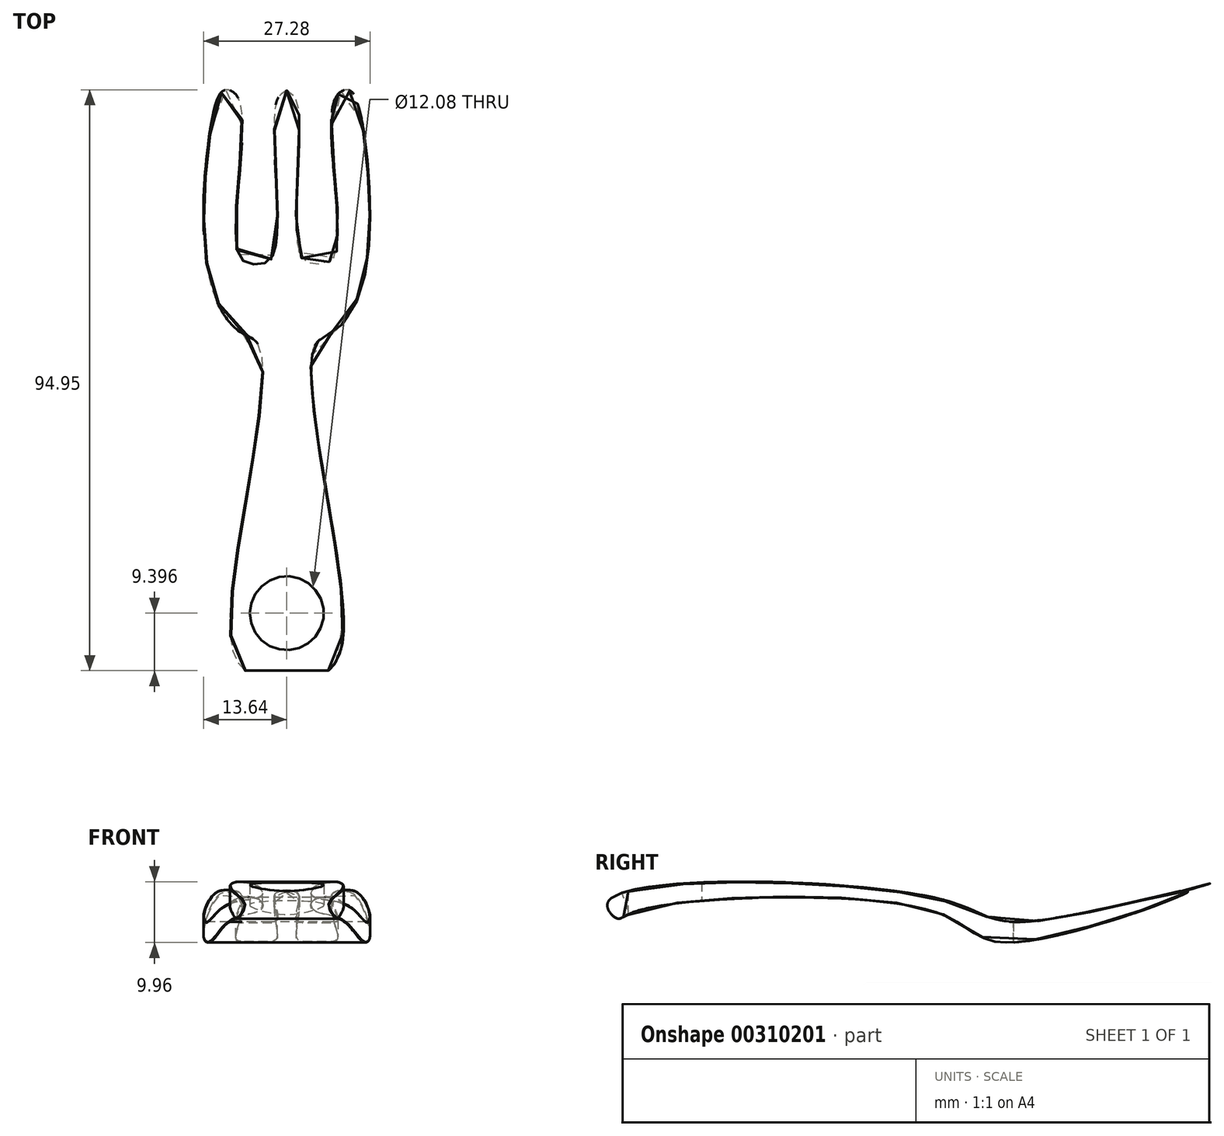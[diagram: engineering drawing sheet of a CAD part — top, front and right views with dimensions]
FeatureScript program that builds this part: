
annotation { "Feature Type Name" : "Feature", "Feature Type Description" : "" }
export const myFeature = defineFeature(function(context is Context, id is Id, definition is map)
    precondition{}
    {
        {
            var Q0;
            Q0=qCreatedBy(makeId("Top.planeOp"),FACE);
            var sketch = newSketch(context, id + "F0", { "sketchPlane" : qUnion([Q0])});
            skLineSegment(sketch, "E0.bottom", {"start": v(15, -50) * mm, "end": v(-15, -50) * mm});
            skLineSegment(sketch, "E0.top", {"start": v(15, 50) * mm, "end": v(-15, 50) * mm});
            skLineSegment(sketch, "E0.left", {"start": v(15, -50) * mm, "end": v(15, 50) * mm});
            skLineSegment(sketch, "E0.right", {"start": v(-15, -50) * mm, "end": v(-15, 50) * mm});
            skPoint(sketch, "E0.middle", {"position": v(0, 0) * mm});
            skSolve(sketch);
        }
        {
            var Q0;
            Q0=makeQuery(id+"F0.imprint","IMPRINT",FACE,{"disambiguationData":[TD([[makeQuery(id+"F0.imprint","IMPRINT",EDGE,{"derivedFrom":sQuery(id+"F0.wireOp",EDGE,"E0.bottom")}),-1.0]])]});
            extrude(context, id + "F1", {"entities" : qUnion([Q0]), "depth" : 30 * mm});
        }
        {
            var Q0;
            Q0=makeQuery(id+"F1.opExtrude","CAP_FACE",FACE,{"disambiguationData":[OSD([sQuery(id+"F0.wireOp",EDGE,"E0.bottom"),sQuery(id+"F0.wireOp",EDGE,"E0.top"),sQuery(id+"F0.wireOp",EDGE,"E0.left"),sQuery(id+"F0.wireOp",EDGE,"E0.right")])],"isStart":false});
            var sketch = newSketch(context, id + "F2", { "sketchPlane" : qUnion([Q0])});
            skFitSpline(sketch, "E1.MirrorCS", {"points": [v(0, 47.97) * mm, v(-1.83, 45.53) * mm, v(-2.18, 21.21) * mm, v(-5.06, 19.56) * mm, v(-7.93, 21.3) * mm, v(-7.58, 45.7) * mm, v(-9.94, 48.05) * mm, v(-11.6, 45.87) * mm, v(-12.99, 18.77) * mm, v(-7.5, 8.4) * mm, v(-4.36, 5.7) * mm, v(-8.88, -33.02) * mm, v(-7.12, -46.63) * mm, v(0, -49.34) * mm], "startDerivative": vector(-53.96, -27.16) * mm, "endDerivative": vector(122.77, -35.87) * mm});
            skLineSegment(sketch, "E2", {"start": v(-15, 50) * mm, "end": v(15, 50) * mm});
            skLineSegment(sketch, "E3", {"start": v(15, 50) * mm, "end": v(15, -50) * mm});
            skLineSegment(sketch, "E4", {"start": v(15, -50) * mm, "end": v(-15, -50) * mm});
            skLineSegment(sketch, "E5", {"start": v(-15, -50) * mm, "end": v(-15, 50) * mm});
            skLineSegment(sketch, "E6", {"start": v(0, 47.97) * mm, "end": v(0, -49.34) * mm});
            skFitSpline(sketch, "E7.MirrorCS", {"points": [v(0, 47.97) * mm, v(1.83, 45.53) * mm, v(2.18, 21.21) * mm, v(5.06, 19.56) * mm, v(7.93, 21.3) * mm, v(7.58, 45.7) * mm, v(9.94, 48.05) * mm, v(11.6, 45.87) * mm, v(12.99, 18.77) * mm, v(7.5, 8.4) * mm, v(4.36, 5.7) * mm, v(8.88, -33.02) * mm, v(7.12, -46.63) * mm, v(0, -49.34) * mm], "startDerivative": vector(53.96, -27.16) * mm, "endDerivative": vector(-122.77, -35.87) * mm});
            skSolve(sketch);
        }
        {
            var Q0;
            Q0=makeQuery(id+"F1.opExtrude","SWEPT_FACE",FACE,{"disambiguationData":[OSD([sQuery(id+"F0.wireOp",EDGE,"E0.left")])]});
            var sketch = newSketch(context, id + "F3", { "sketchPlane" : qUnion([Q0])});
            skLineSegment(sketch, "E8.bottom", {"start": v(0, 30) * mm, "end": v(0, 30) * mm});
            skLineSegment(sketch, "E8.top", {"start": v(0, -30) * mm, "end": v(0, -30) * mm});
            skLineSegment(sketch, "E8.left", {"start": v(0, 30) * mm, "end": v(0, -30) * mm, "construction": true});
            skLineSegment(sketch, "E8.right", {"start": v(0, 30) * mm, "end": v(0, -30) * mm, "construction": true});
            skPoint(sketch, "E8.middle", {"position": v(0, 0) * mm});
            skLineSegment(sketch, "E9.bottom", {"start": v(48.41, 6.93) * mm, "end": v(-48.41, 6.93) * mm, "construction": true});
            skLineSegment(sketch, "E9.top", {"start": v(48.41, 22.97) * mm, "end": v(-48.41, 22.97) * mm, "construction": true});
            skLineSegment(sketch, "E9.left", {"start": v(48.41, 6.93) * mm, "end": v(48.41, 22.97) * mm, "construction": true});
            skLineSegment(sketch, "E9.right", {"start": v(-48.41, 6.93) * mm, "end": v(-48.41, 22.97) * mm, "construction": true});
            skPoint(sketch, "E9.middle", {"position": v(0, 14.95) * mm});
            skPoint(sketch, "E10.5.internal.snap0", {"position": v(48.41, 14.95) * mm});
            skFitSpline(sketch, "E10", {"points": [v(48.41, 18.45) * mm, v(21.04, 13.32) * mm, v(7.46, 17.07) * mm, v(-46.65, 16.75) * mm, v(-45.4, 13.9) * mm, v(-42.5, 14.95) * mm, v(6.64, 14.95) * mm, v(18.7, 9.92) * mm, v(48.41, 18.45) * mm]});
            skSolve(sketch);
        }
        {
            var Q0;
            Q0=makeQuery(id+"F3.imprint","IMPRINT",FACE,{"disambiguationData":[TD([[makeQuery(id+"F3.imprint","IMPRINT",EDGE,{"derivedFrom":sQuery(id+"F3.wireOp",EDGE,"E10")}),-1.0]])]});
            extrude(context, id + "F4", {"entities" : qUnion([Q0]), "operationType" : NewBodyOperationType.REMOVE, "oppositeDirection" : true, "depth" : 30 * mm});
        }
        {
            var Q0;
            Q0=makeQuery(id+"F2.imprint","IMPRINT",FACE,{"disambiguationData":[TD([[makeQuery(id+"F2.imprint","IMPRINT",EDGE,{"derivedFrom":sQuery(id+"F2.wireOp",EDGE,"E1.MirrorCS")}),-1.0]])]});
            extrude(context, id + "F5", {"entities" : qUnion([Q0]), "operationType" : NewBodyOperationType.REMOVE, "oppositeDirection" : true, "depth" : 30 * mm});
        }
        {
            var Q0;
            Q0=makeQuery(id+"F5.boolean.opBoolean","INTERSECT",EDGE,{"derivedFrom":[makeQuery(id+"F4.boolean.opBoolean","COPY",FACE,{"derivedFrom":makeQuery(id+"F4.opExtrude","SWEPT_FACE",FACE,{"disambiguationData":[OSD([sQuery(id+"F3.wireOp",EDGE,"E10")])]})}),makeQuery(id+"F5.opExtrude","SWEPT_FACE",FACE,{"disambiguationData":[OSD([sQuery(id+"F2.wireOp",EDGE,"E7.MirrorCS")])]})]});
            var Q1;
            Q1=makeQuery(id+"F5.boolean.opBoolean","INTERSECT",EDGE,{"derivedFrom":[makeQuery(id+"F4.boolean.opBoolean","COPY",FACE,{"derivedFrom":makeQuery(id+"F4.opExtrude","SWEPT_FACE",FACE,{"disambiguationData":[OSD([sQuery(id+"F3.wireOp",EDGE,"E10")])]})}),makeQuery(id+"F5.opExtrude","SWEPT_FACE",FACE,{"disambiguationData":[OSD([sQuery(id+"F2.wireOp",EDGE,"E1.MirrorCS")])]})]});
            fillet(context, id + "F6", {"entities" : qUnion([Q0, Q1]), "radius" : .1 * mm, "tangentPropagation" : true, "allowEdgeOverflow" : false});
        }
        {
            var Q0;
            Q0=qCreatedBy(makeId("Top.planeOp"),FACE);
            var sketch = newSketch(context, id + "F7", { "sketchPlane" : qUnion([Q0])});
            skCircle(sketch, "E11", {"center": v(0, -37.5) * mm, "radius": 6.04 * mm});
            skSolve(sketch);
        }
        {
            var Q0;
            Q0=makeQuery(id+"F7.imprint","IMPRINT",FACE,{"disambiguationData":[TD([[makeQuery(id+"F7.imprint","IMPRINT",EDGE,{"derivedFrom":sQuery(id+"F7.wireOp",EDGE,"E11")}),1.0]])]});
            extrude(context, id + "F8", {"entities" : qUnion([Q0]), "operationType" : NewBodyOperationType.REMOVE, "depth" : 35.5 * mm});
        }
    });
